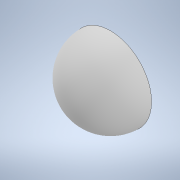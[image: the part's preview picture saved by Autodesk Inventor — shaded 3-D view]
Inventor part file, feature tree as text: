
AUTODESK INVENTOR PART (.ipt)
format: ipt  version: 2022 (Build 260153000, 153)  size: 120,832 bytes
history: native  units: in
note: dims shown in document units (in); Inventor stores cm internally (conversion verified against a paired STEP export)
features: sketch x2, revolve x1, extrude x1
ambient origin geometry x8: Origin, YZ Plane, XZ Plane, XY Plane, X Axis, Y Axis, Z Axis, Center Point
bodies: Solid2 (feature_tree)
feature tree (4):
  revolve  "Revolution1"  Angle=180.0deg
  extrude  "Extrusion1"  Depth=0.125in TaperAngle=0.0deg
  sketch  "Sketch1"  dims[d0=0.5in d1=180.0deg]
  sketch  "Sketch2"  dims[d2=0.1in d3=0.125in d4=0.0in]
